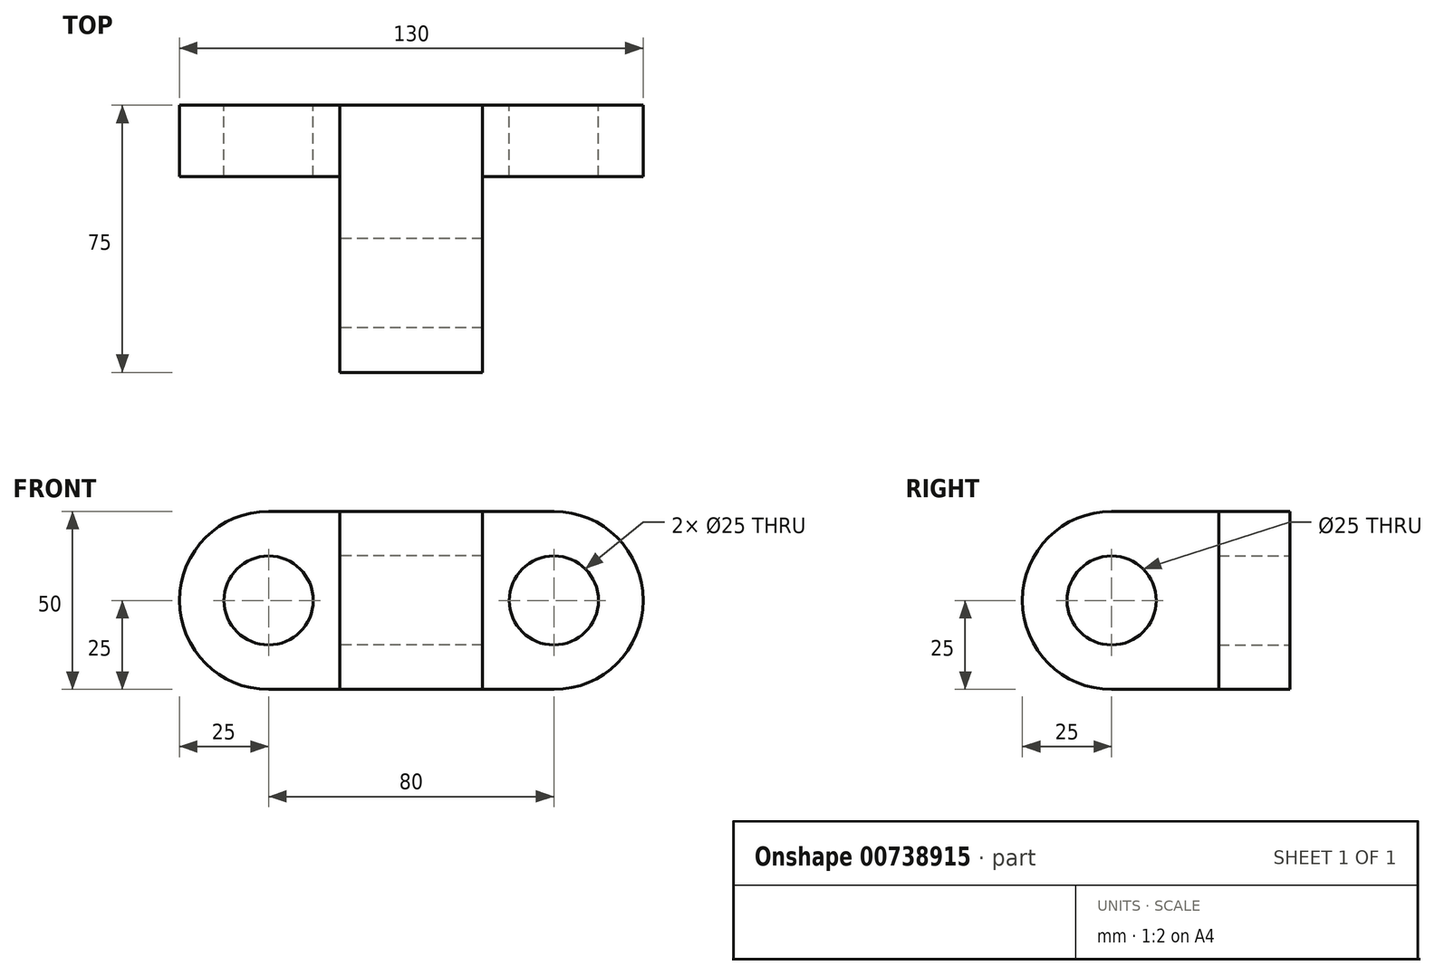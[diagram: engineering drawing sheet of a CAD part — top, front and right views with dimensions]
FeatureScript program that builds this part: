
annotation { "Feature Type Name" : "Feature", "Feature Type Description" : "" }
export const myFeature = defineFeature(function(context is Context, id is Id, definition is map)
    precondition{}
    {
        {
            var Q0;
            Q0=qCreatedBy(makeId("Front.planeOp"),FACE);
            var sketch = newSketch(context, id + "F0", { "sketchPlane" : qUnion([Q0])});
            skArc(sketch, "E0", {"start": v(0, 50) * mm, "mid": v(-25, 25) * mm, "end": v(0, 0) * mm});
            skLineSegment(sketch, "E1", {"start": v(0, 50) * mm, "end": v(20, 50) * mm});
            skLineSegment(sketch, "E2", {"start": v(0, 0) * mm, "end": v(20, 0) * mm});
            skLineSegment(sketch, "E3.bottom", {"start": v(20, 50) * mm, "end": v(60, 50) * mm});
            skLineSegment(sketch, "E3.top", {"start": v(20, 0) * mm, "end": v(60, 0) * mm});
            skLineSegment(sketch, "E3.left", {"start": v(20, 50) * mm, "end": v(20, 0) * mm});
            skLineSegment(sketch, "E3.right", {"start": v(60, 50) * mm, "end": v(60, 0) * mm});
            skLineSegment(sketch, "E4", {"start": v(60, 50) * mm, "end": v(80, 50) * mm});
            skLineSegment(sketch, "E5", {"start": v(60, 0) * mm, "end": v(80, 0) * mm});
            skArc(sketch, "E6", {"start": v(80, 0) * mm, "mid": v(105, 25) * mm, "end": v(80, 50) * mm});
            skCircle(sketch, "E7", {"center": v(0, 25) * mm, "radius": 12.5 * mm});
            skCircle(sketch, "E8", {"center": v(80, 25) * mm, "radius": 12.5 * mm});
            skSolve(sketch);
        }
        {
            var Q0;
            Q0=makeQuery(id+"F0.imprint","IMPRINT",FACE,{"disambiguationData":[TD([[makeQuery(id+"F0.imprint","IMPRINT",EDGE,{"derivedFrom":sQuery(id+"F0.wireOp",EDGE,"E0")}),1.0]])]});
            var Q1;
            Q1=makeQuery(id+"F0.imprint","IMPRINT",FACE,{"disambiguationData":[TD([[makeQuery(id+"F0.imprint","IMPRINT",EDGE,{"derivedFrom":sQuery(id+"F0.wireOp",EDGE,"E3.right")}),1.0]])]});
            extrude(context, id + "F1", {"entities" : qUnion([Q0, Q1]), "depth" : 20 * mm, "offsetDistance" : 25 * mm});
        }
        {
            var Q0;
            Q0=makeQuery(id+"F0.imprint","IMPRINT",FACE,{"disambiguationData":[TD([[makeQuery(id+"F0.imprint","IMPRINT",EDGE,{"derivedFrom":sQuery(id+"F0.wireOp",EDGE,"E3.bottom")}),-1.0]])]});
            extrude(context, id + "F2", {"entities" : qUnion([Q0]), "depth" : 50 * mm, "offsetDistance" : 25 * mm});
        }
        {
            var Q0;
            Q0=makeQuery(id+"F2.opExtrude","SWEPT_FACE",FACE,{"disambiguationData":[OSD([sQuery(id+"F0.wireOp",EDGE,"E3.left")])]});
            var sketch = newSketch(context, id + "F3", { "sketchPlane" : qUnion([Q0])});
            skArc(sketch, "E9", {"start": v(50, 0) * mm, "mid": v(75, 25) * mm, "end": v(50, 50) * mm});
            skCircle(sketch, "E10", {"center": v(50, 25) * mm, "radius": 12.5 * mm});
            skSolve(sketch);
        }
        {
            var Q0;
            {var subQ0=sQuery(id+"F3.wireOp",EDGE,"E10");var subQ1=makeQuery(id+"F2.opExtrude","CAP_EDGE",EDGE,{"disambiguationData":[OSD([sQuery(id+"F0.wireOp",EDGE,"E3.left")])],"isStart":false});var subQ2=makeQuery(id+"F3.imprint","INTERSECT",VERTEX,{"disambiguationData":[OD(0.0)],"derivedFrom":[subQ1,subQ0]});Q0=makeQuery(id+"F3.imprint","IMPRINT",FACE,{"disambiguationData":[TD([[makeQuery(id+"F3.imprint","IMPRINT",EDGE,{"disambiguationData":[TD([[subQ2,-1.0]])],"derivedFrom":subQ0}),1.0]])]});}
            var Q1;
            {var subQ0=sQuery(id+"F3.wireOp",EDGE,"E9");Q1=makeQuery(id+"F3.imprint","IMPRINT",FACE,{"disambiguationData":[TD([[makeQuery(id+"F3.imprint","IMPRINT",EDGE,{"derivedFrom":subQ0}),1.0]])]});}
            var Q2;
            Q2=makeQuery(id+"F2.opExtrude","SWEPT_FACE",FACE,{"disambiguationData":[OSD([sQuery(id+"F0.wireOp",EDGE,"E3.right")])]});
            extrude(context, id + "F4", {"entities" : qUnion([Q0, Q1]), "operationType" : NewBodyOperationType.ADD, "endBound" : BoundingType.UP_TO_SURFACE, "oppositeDirection" : true, "depth" : 25 * mm, "endBoundEntityFace" : qUnion([Q2]), "offsetDistance" : 25 * mm});
        }
        {
            var Q0;
            {var subQ0=sQuery(id+"F3.wireOp",EDGE,"E10");var subQ1=makeQuery(id+"F2.opExtrude","CAP_EDGE",EDGE,{"disambiguationData":[OSD([sQuery(id+"F0.wireOp",EDGE,"E3.left")])],"isStart":false});var subQ2=makeQuery(id+"F3.imprint","INTERSECT",VERTEX,{"disambiguationData":[OD(0.0)],"derivedFrom":[subQ1,subQ0]});Q0=makeQuery(id+"F3.imprint","IMPRINT",FACE,{"disambiguationData":[TD([[makeQuery(id+"F3.imprint","IMPRINT",EDGE,{"disambiguationData":[TD([[subQ2,-1.0]])],"derivedFrom":subQ0}),1.0]])]});}
            var Q1;
            {var subQ0=sQuery(id+"F0.wireOp",EDGE,"E3.right");Q1=makeQuery(id+"F4.boolean.opBoolean","MERGE",FACE,{"derivedFrom":[makeQuery(id+"F2.opExtrude","SWEPT_FACE",FACE,{"disambiguationData":[OSD([subQ0])]}),makeQuery(id+"F4.opExtrude","CAP_FACE",FACE,{"disambiguationData":[OSD([subQ0]),OD(0.0)],"isStart":false})]});}
            extrude(context, id + "F5", {"entities" : qUnion([Q0]), "operationType" : NewBodyOperationType.REMOVE, "endBound" : BoundingType.THROUGH_ALL, "oppositeDirection" : true, "depth" : 25 * mm, "endBoundEntityFace" : qUnion([Q1]), "offsetDistance" : 25 * mm});
        }
    });
